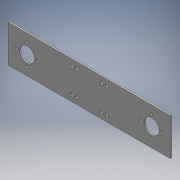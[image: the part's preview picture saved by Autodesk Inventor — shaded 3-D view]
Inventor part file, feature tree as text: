
AUTODESK INVENTOR PART (.ipt)
format: ipt  version: 2016 (Build 200138000, 138)  size: 148,992 bytes
history: native  units: mm
features: extrude x3, sketch x3, other x1
ambient origin geometry x8: Origin, YZ Plane, XZ Plane, XY Plane, X Axis, Y Axis, Z Axis, Center Point
bodies: Body1 (feature_tree)
feature tree (7):
  other  "ソリッド1"
  extrude  "押し出し1"  Depth=260.0mm
  extrude  "押し出し2"  Depth=60.0mm
  extrude  "押し出し3"  Depth=158.0mm
  sketch  "スケッチ1"
  sketch  "スケッチ2"
  sketch  "スケッチ3"
